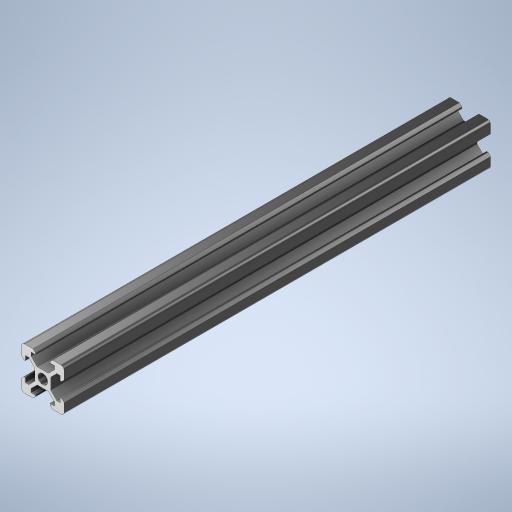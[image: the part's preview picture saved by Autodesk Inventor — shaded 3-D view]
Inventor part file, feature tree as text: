
AUTODESK INVENTOR PART (.ipt)
format: ipt  version: 2024.2 (Build 282272000, 272)  size: 514,048 bytes
history: native  units: mm
features: extrude x1, pattern_circular x1, chamfer x1, fillet x1, sketch x1, other x1
ambient origin geometry x8: Origin, YZ Plane, XZ Plane, XY Plane, X Axis, Y Axis, Z Axis, Center Point
bodies: Solid1 (feature_tree)
feature tree (6):
  extrude  "Extrusion1"  TaperAngle=135.0deg  [1 undecoded]
  pattern_circular  "Circular Pattern1"  Count=2  [1 undecoded]
  chamfer  "Chamfer1"  Distance=200.0mm
  fillet  "Fillet1"  Radius=40.0mm
  sketch  "Sketch1"  dims[d0=1.5mm d6=6.3mm d9=4.6mm d18=135.0deg d22=20.0mm d24=200.0mm d25=0.0mm d26=40.0mm d27=360.0deg d34=11.0mm d35=6.79mm d36=1.8mm d37=1.185mm d38=2.0mm d39=45.0deg d40=1.5mm]
  other  "Image1"
note: 2 required parameter values undecoded (feature->parameter linkage not recoverable at this tier; creation-order binding heuristic only, values carry confidence <= 0.55)
